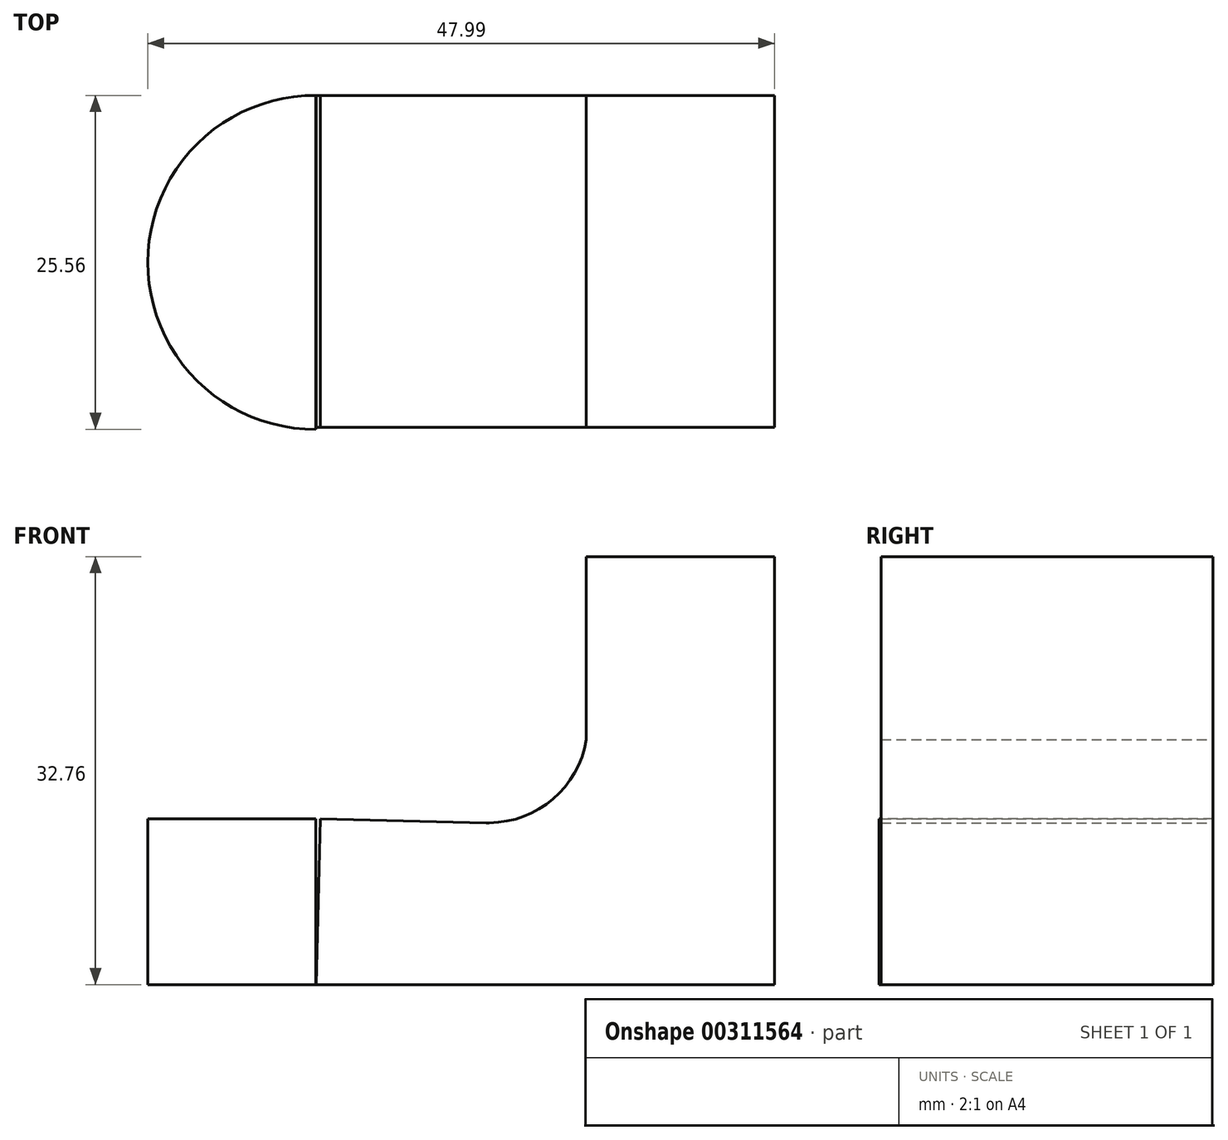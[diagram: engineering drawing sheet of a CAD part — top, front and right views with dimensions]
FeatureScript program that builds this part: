
annotation { "Feature Type Name" : "Feature", "Feature Type Description" : "" }
export const myFeature = defineFeature(function(context is Context, id is Id, definition is map)
    precondition{}
    {
        {
            var Q0;
            Q0=qCreatedBy(makeId("Front.planeOp"),FACE);
            var sketch = newSketch(context, id + "F0", { "sketchPlane" : qUnion([Q0])});
            skLineSegment(sketch, "E0.bottom", {"start": v(0, 0) * mm, "end": v(-33.1, 0) * mm});
            skLineSegment(sketch, "E0.left", {"start": v(0, 0) * mm, "end": v(0, 5.48) * mm});
            skLineSegment(sketch, "E0.right", {"start": v(-33.1, 0) * mm, "end": v(-33.1, 5.48) * mm});
            skLineSegment(sketch, "E1.top", {"start": v(0, 52.6) * mm, "end": v(-6.3, 52.6) * mm});
            skLineSegment(sketch, "E1.left", {"start": v(0, 5.48) * mm, "end": v(0, 52.6) * mm});
            skArc(sketch, "E2", {"start": v(-11.78, 5.48) * mm, "mid": v(-8.08, 7.54) * mm, "end": v(-6.3, 11.37) * mm});
            skLineSegment(sketch, "E3", {"start": v(-6.3, 52.6) * mm, "end": v(-6.3, 11.37) * mm});
            skLineSegment(sketch, "E4", {"start": v(-33.1, 5.48) * mm, "end": v(-11.78, 5.48) * mm});
            skSolve(sketch);
        }
        {
            var Q0;
            Q0=qCreatedBy(makeId("Top.planeOp"),FACE);
            var sketch = newSketch(context, id + "F1", { "sketchPlane" : qUnion([Q0])});
            skSolve(sketch);
        }
        {
            var Q0;
            Q0=qCreatedBy(makeId("Front.planeOp"),FACE);
            var sketch = newSketch(context, id + "F2", { "sketchPlane" : qUnion([Q0])});
            skLineSegment(sketch, "E5", {"start": v(-35.11, 0) * mm, "end": v(0, 0) * mm});
            skLineSegment(sketch, "E6", {"start": v(0, 0) * mm, "end": v(0, 32.76) * mm});
            skLineSegment(sketch, "E7", {"start": v(0, 32.76) * mm, "end": v(-14.42, 32.76) * mm});
            skLineSegment(sketch, "E8", {"start": v(-34.8, 12.7) * mm, "end": v(-35.11, 0) * mm});
            skLineSegment(sketch, "E9", {"start": v(-14.42, 32.76) * mm, "end": v(-14.42, 21.24) * mm});
            skLineSegment(sketch, "E10", {"start": v(-34.8, 12.7) * mm, "end": v(-22.08, 12.38) * mm});
            skLineSegment(sketch, "E11", {"start": v(-14.42, 21.24) * mm, "end": v(-14.42, 12.46) * mm});
            skLineSegment(sketch, "E12", {"start": v(-14.42, 12.46) * mm, "end": v(-21.84, 12.38) * mm});
            skPoint(sketch, "E13.visualSharp", {"position": v(-21.96, 12.38) * mm});
            skArc(sketch, "E13.filletArc", {"start": v(-22.08, 12.38) * mm, "mid": v(-21.96, 12.38) * mm, "end": v(-21.84, 12.38) * mm});
            skArc(sketch, "E14", {"start": v(-21.84, 12.38) * mm, "mid": v(-16.1, 15.1) * mm, "end": v(-14.42, 21.24) * mm});
            skSolve(sketch);
        }
        {
            var Q0;
            Q0 = qSketchRegion(id + "F2", true);
            extrude(context, id + "F3", {"entities" : qUnion([Q0]), "depth" : 25.4 * mm});
        }
        {
            var Q0;
            Q0=qCreatedBy(makeId("Top.planeOp"),FACE);
            var sketch = newSketch(context, id + "F4", { "sketchPlane" : qUnion([Q0])});
            skArc(sketch, "E15", {"start": v(-35.11, 0) * mm, "mid": v(-47.99, -12.78) * mm, "end": v(-35.11, -25.56) * mm});
            skLineSegment(sketch, "E16", {"start": v(-35.11, 0) * mm, "end": v(-35.11, -25.56) * mm});
            skSolve(sketch);
        }
        {
            var Q0;
            Q0 = qSketchRegion(id + "F4", true);
            extrude(context, id + "F5", {"entities" : qUnion([Q0]), "operationType" : NewBodyOperationType.ADD, "depth" : 12.7 * mm});
        }
        {
            var Q0;
            Q0 = qSketchRegion(id + "F4", true);
            extrude(context, id + "F6", {"entities" : qUnion([Q0]), "depth" : 12.7 * mm});
        }
        {
            var Q0;
            Q0 = qSketchRegion(id + "F4", true);
            extrude(context, id + "F7", {"entities" : qUnion([Q0]), "depth" : 12.7 * mm});
        }
    });
